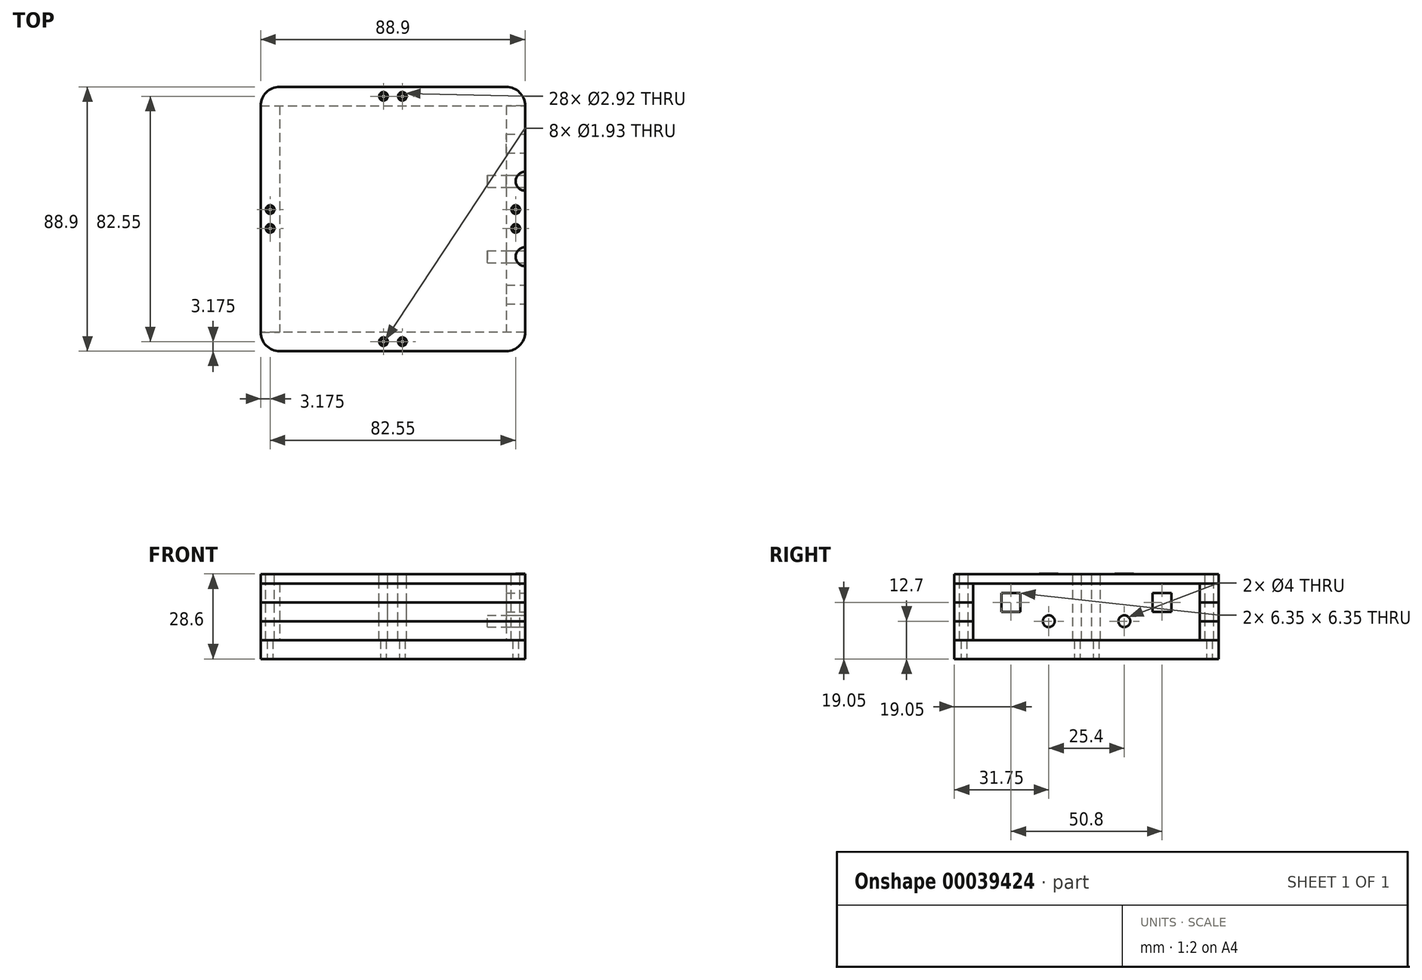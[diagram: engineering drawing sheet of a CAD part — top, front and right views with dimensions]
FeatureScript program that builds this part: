
annotation { "Feature Type Name" : "Feature", "Feature Type Description" : "" }
export const myFeature = defineFeature(function(context is Context, id is Id, definition is map)
    precondition{}
    {
        {
            var Q0;
            Q0=qCreatedBy(makeId("Top.planeOp"),FACE);
            var sketch = newSketch(context, id + "F0", { "sketchPlane" : qUnion([Q0])});
            skLineSegment(sketch, "E0.rect.bottom", {"start": v(38.1, 44.45) * mm, "end": v(-38.1, 44.45) * mm});
            skLineSegment(sketch, "E0.rect.top", {"start": v(38.1, -44.45) * mm, "end": v(-38.1, -44.45) * mm});
            skLineSegment(sketch, "E0.rect.left", {"start": v(44.45, 38.1) * mm, "end": v(44.45, -38.1) * mm});
            skLineSegment(sketch, "E0.rect.right", {"start": v(-44.45, 38.1) * mm, "end": v(-44.45, -38.1) * mm});
            skPoint(sketch, "E0.rect.middle", {"position": v(0, 0) * mm});
            skPoint(sketch, "E1.visualSharp", {"position": v(-44.45, 44.45) * mm});
            skArc(sketch, "E1.filletArc", {"start": v(-38.1, 44.45) * mm, "mid": v(-42.6, 42.6) * mm, "end": v(-44.45, 38.1) * mm});
            skPoint(sketch, "E2.visualSharp", {"position": v(44.45, 44.45) * mm});
            skArc(sketch, "E2.filletArc", {"start": v(44.45, 38.1) * mm, "mid": v(42.6, 42.6) * mm, "end": v(38.1, 44.45) * mm});
            skPoint(sketch, "E3.visualSharp", {"position": v(44.45, -44.45) * mm});
            skArc(sketch, "E3.filletArc", {"start": v(38.1, -44.45) * mm, "mid": v(42.6, -42.6) * mm, "end": v(44.45, -38.1) * mm});
            skPoint(sketch, "E4.visualSharp", {"position": v(-44.45, -44.45) * mm});
            skArc(sketch, "E4.filletArc", {"start": v(-44.45, -38.1) * mm, "mid": v(-42.6, -42.6) * mm, "end": v(-38.1, -44.45) * mm});
            skSolve(sketch);
        }
        {
            var Q0;
            Q0 = qSketchRegion(id + "F0", true);
            extrude(context, id + "F1", {"entities" : qUnion([Q0]), "depth" : 6.35 * mm});
        }
        {
            var Q0;
            Q0=makeQuery(id+"F1.opExtrude","CAP_FACE",FACE,{"disambiguationData":[OSD([sQuery(id+"F0.wireOp",EDGE,"E0.rect.bottom"),sQuery(id+"F0.wireOp",EDGE,"E0.rect.top"),sQuery(id+"F0.wireOp",EDGE,"E0.rect.left"),sQuery(id+"F0.wireOp",EDGE,"E0.rect.right"),sQuery(id+"F0.wireOp",EDGE,"E1.filletArc"),sQuery(id+"F0.wireOp",EDGE,"E2.filletArc"),sQuery(id+"F0.wireOp",EDGE,"E3.filletArc"),sQuery(id+"F0.wireOp",EDGE,"E4.filletArc")])],"isStart":false});
            var sketch = newSketch(context, id + "F2", { "sketchPlane" : qUnion([Q0])});
            skLineSegment(sketch, "E5.bottom", {"start": v(-44.45, 38.1) * mm, "end": v(-38.1, 38.1) * mm});
            skLineSegment(sketch, "E5.top", {"start": v(-44.45, -38.1) * mm, "end": v(-38.1, -38.1) * mm});
            skLineSegment(sketch, "E5.left", {"start": v(-44.45, 38.1) * mm, "end": v(-44.45, -38.1) * mm});
            skLineSegment(sketch, "E5.right", {"start": v(-38.1, 38.1) * mm, "end": v(-38.1, -38.1) * mm});
            skLineSegment(sketch, "E6.bottom", {"start": v(44.45, 38.1) * mm, "end": v(38.1, 38.1) * mm});
            skLineSegment(sketch, "E6.top", {"start": v(44.45, -38.1) * mm, "end": v(38.1, -38.1) * mm});
            skLineSegment(sketch, "E6.left", {"start": v(44.45, 38.1) * mm, "end": v(44.45, -38.1) * mm});
            skLineSegment(sketch, "E6.right", {"start": v(38.1, 38.1) * mm, "end": v(38.1, -38.1) * mm});
            skSolve(sketch);
        }
        {
            var Q0;
            Q0 = qSketchRegion(id + "F2", true);
            extrude(context, id + "F3", {"entities" : qUnion([Q0]), "depth" : 19.05 * mm});
        }
        {
            var Q0;
            Q0=makeQuery(id+"F1.opExtrude","CAP_FACE",FACE,{"disambiguationData":[OSD([sQuery(id+"F0.wireOp",EDGE,"E0.rect.bottom"),sQuery(id+"F0.wireOp",EDGE,"E0.rect.top"),sQuery(id+"F0.wireOp",EDGE,"E0.rect.left"),sQuery(id+"F0.wireOp",EDGE,"E0.rect.right"),sQuery(id+"F0.wireOp",EDGE,"E1.filletArc"),sQuery(id+"F0.wireOp",EDGE,"E2.filletArc"),sQuery(id+"F0.wireOp",EDGE,"E3.filletArc"),sQuery(id+"F0.wireOp",EDGE,"E4.filletArc")])],"isStart":false});
            var sketch = newSketch(context, id + "F4", { "sketchPlane" : qUnion([Q0])});
            skArc(sketch, "E7.0", {"start": v(-38.1, 44.45) * mm, "mid": v(-42.6, 42.6) * mm, "end": v(-44.45, 38.1) * mm});
            skLineSegment(sketch, "E8.0", {"start": v(38.1, 44.45) * mm, "end": v(-38.1, 44.45) * mm});
            skArc(sketch, "E9.0", {"start": v(44.45, 38.1) * mm, "mid": v(42.6, 42.6) * mm, "end": v(38.1, 44.45) * mm});
            skLineSegment(sketch, "E10", {"start": v(-38.1, 38.1) * mm, "end": v(38.1, 38.1) * mm});
            skLineSegment(sketch, "E11.0", {"start": v(-44.45, -38.1) * mm, "end": v(-38.1, -38.1) * mm});
            skArc(sketch, "E12.0", {"start": v(-44.45, -38.1) * mm, "mid": v(-42.6, -42.6) * mm, "end": v(-38.1, -44.45) * mm});
            skLineSegment(sketch, "E13.0", {"start": v(38.1, -44.45) * mm, "end": v(-38.1, -44.45) * mm});
            skArc(sketch, "E14.0", {"start": v(38.1, -44.45) * mm, "mid": v(42.6, -42.6) * mm, "end": v(44.45, -38.1) * mm});
            skLineSegment(sketch, "E15", {"start": v(-38.1, -38.1) * mm, "end": v(38.1, -38.1) * mm});
            skLineSegment(sketch, "E16", {"start": v(38.1, -38.1) * mm, "end": v(44.45, -38.1) * mm});
            skLineSegment(sketch, "E17", {"start": v(-38.1, -38.1) * mm, "end": v(-44.45, -38.1) * mm});
            skLineSegment(sketch, "E18", {"start": v(-44.45, 38.1) * mm, "end": v(-38.1, 38.1) * mm});
            skLineSegment(sketch, "E19", {"start": v(38.1, 38.1) * mm, "end": v(44.45, 38.1) * mm});
            skSolve(sketch);
        }
        {
            var Q0;
            Q0 = qSketchRegion(id + "F4", true);
            extrude(context, id + "F5", {"entities" : qUnion([Q0]), "depth" : 12.7 * mm});
        }
        {
            var Q0;
            Q0=makeQuery(id+"F5.opExtrude","CAP_FACE",FACE,{"disambiguationData":[OSD([sQuery(id+"F4.wireOp",EDGE,"E7.0"),sQuery(id+"F4.wireOp",EDGE,"E8.0"),sQuery(id+"F4.wireOp",EDGE,"E9.0"),sQuery(id+"F4.wireOp",EDGE,"E10"),sQuery(id+"F4.wireOp",EDGE,"E18"),sQuery(id+"F4.wireOp",EDGE,"E19")])],"isStart":false});
            var sketch = newSketch(context, id + "F6", { "sketchPlane" : qUnion([Q0])});
            skLineSegment(sketch, "E20.0.0", {"start": v(-44.45, 38.1) * mm, "end": v(44.45, 38.1) * mm});
            skArc(sketch, "E20.0.1", {"start": v(44.45, 38.1) * mm, "mid": v(42.6, 42.6) * mm, "end": v(38.1, 44.45) * mm});
            skLineSegment(sketch, "E20.0.2", {"start": v(38.1, 44.45) * mm, "end": v(-38.1, 44.45) * mm});
            skArc(sketch, "E20.0.3", {"start": v(-38.1, 44.45) * mm, "mid": v(-42.6, 42.6) * mm, "end": v(-44.45, 38.1) * mm});
            skLineSegment(sketch, "E21.0.0", {"start": v(44.45, -38.1) * mm, "end": v(-44.45, -38.1) * mm});
            skArc(sketch, "E21.0.1", {"start": v(-44.45, -38.1) * mm, "mid": v(-42.6, -42.6) * mm, "end": v(-38.1, -44.45) * mm});
            skLineSegment(sketch, "E21.0.2", {"start": v(-38.1, -44.45) * mm, "end": v(38.1, -44.45) * mm});
            skArc(sketch, "E21.0.3", {"start": v(38.1, -44.45) * mm, "mid": v(42.6, -42.6) * mm, "end": v(44.45, -38.1) * mm});
            skSolve(sketch);
        }
        {
            var Q0;
            Q0 = qSketchRegion(id + "F6", true);
            extrude(context, id + "F7", {"entities" : qUnion([Q0]), "depth" : 6.35 * mm});
        }
        {
            var Q0;
            Q0=makeQuery(id+"F3.opExtrude","CAP_FACE",FACE,{"disambiguationData":[OSD([sQuery(id+"F2.wireOp",EDGE,"E5.bottom"),sQuery(id+"F2.wireOp",EDGE,"E5.top"),sQuery(id+"F2.wireOp",EDGE,"E5.left"),sQuery(id+"F2.wireOp",EDGE,"E5.right")])],"isStart":false});
            var sketch = newSketch(context, id + "F8", { "sketchPlane" : qUnion([Q0])});
            skArc(sketch, "E22.0.0", {"start": v(44.45, 38.1) * mm, "mid": v(42.6, 42.6) * mm, "end": v(38.1, 44.45) * mm});
            skLineSegment(sketch, "E22.0.1", {"start": v(38.1, 44.45) * mm, "end": v(-38.1, 44.45) * mm});
            skArc(sketch, "E22.0.2", {"start": v(-38.1, 44.45) * mm, "mid": v(-42.6, 42.6) * mm, "end": v(-44.45, 38.1) * mm});
            skLineSegment(sketch, "E22.0.3", {"start": v(-44.45, 38.1) * mm, "end": v(-44.45, -38.1) * mm});
            skArc(sketch, "E22.0.4", {"start": v(-44.45, -38.1) * mm, "mid": v(-42.6, -42.6) * mm, "end": v(-38.1, -44.45) * mm});
            skLineSegment(sketch, "E22.0.5", {"start": v(-38.1, -44.45) * mm, "end": v(38.1, -44.45) * mm});
            skArc(sketch, "E22.0.6", {"start": v(38.1, -44.45) * mm, "mid": v(42.6, -42.6) * mm, "end": v(44.45, -38.1) * mm});
            skLineSegment(sketch, "E22.0.7", {"start": v(44.45, -38.1) * mm, "end": v(44.45, 38.1) * mm});
            skSolve(sketch);
        }
        {
            var Q0;
            Q0 = qSketchRegion(id + "F8", true);
            extrude(context, id + "F9", {"entities" : qUnion([Q0]), "depth" : 3.17 * mm});
        }
        {
            var Q0;
            Q0=makeQuery(id+"F3.opExtrude","SWEPT_FACE",FACE,{"disambiguationData":[OSD([sQuery(id+"F2.wireOp",EDGE,"E6.left")])]});
            var sketch = newSketch(context, id + "F10", { "sketchPlane" : qUnion([Q0])});
            skLineSegment(sketch, "E23.rect.bottom", {"start": v(22.22, 22.23) * mm, "end": v(28.57, 22.23) * mm});
            skLineSegment(sketch, "E23.rect.top", {"start": v(22.22, 15.88) * mm, "end": v(28.57, 15.88) * mm});
            skLineSegment(sketch, "E23.rect.left", {"start": v(22.22, 22.23) * mm, "end": v(22.22, 15.88) * mm});
            skLineSegment(sketch, "E23.rect.right", {"start": v(28.57, 22.23) * mm, "end": v(28.57, 15.88) * mm});
            skPoint(sketch, "E23.rect.middle", {"position": v(25.4, 19.05) * mm});
            skLineSegment(sketch, "E24.rect.bottom", {"start": v(-22.22, 15.88) * mm, "end": v(-28.57, 15.88) * mm});
            skLineSegment(sketch, "E24.rect.top", {"start": v(-22.22, 22.23) * mm, "end": v(-28.57, 22.23) * mm});
            skLineSegment(sketch, "E24.rect.left", {"start": v(-22.22, 15.88) * mm, "end": v(-22.22, 22.23) * mm});
            skLineSegment(sketch, "E24.rect.right", {"start": v(-28.57, 15.88) * mm, "end": v(-28.57, 22.23) * mm});
            skPoint(sketch, "E24.rect.middle", {"position": v(-25.4, 19.05) * mm});
            skCircle(sketch, "E25", {"center": v(-12.7, 12.7) * mm, "radius": 2 * mm});
            skCircle(sketch, "E26", {"center": v(12.7, 12.7) * mm, "radius": 2 * mm});
            skLineSegment(sketch, "E27", {"start": v(0, 25.4) * mm, "end": v(0, 6.35) * mm});
            skSolve(sketch);
        }
        {
            var Q0;
            Q0 = qSketchRegion(id + "F10", true);
            extrude(context, id + "F11", {"entities" : qUnion([Q0]), "operationType" : NewBodyOperationType.REMOVE, "oppositeDirection" : true, "depth" : 25.4 * mm});
        }
        {
            var Q0;
            Q0=makeQuery(id+"F9.opExtrude","CAP_FACE",FACE,{"disambiguationData":[OSD([sQuery(id+"F8.wireOp",EDGE,"E22.0.0"),sQuery(id+"F8.wireOp",EDGE,"E22.0.1"),sQuery(id+"F8.wireOp",EDGE,"E22.0.2"),sQuery(id+"F8.wireOp",EDGE,"E22.0.3"),sQuery(id+"F8.wireOp",EDGE,"E22.0.4"),sQuery(id+"F8.wireOp",EDGE,"E22.0.5"),sQuery(id+"F8.wireOp",EDGE,"E22.0.6"),sQuery(id+"F8.wireOp",EDGE,"E22.0.7")])],"isStart":false});
            var sketch = newSketch(context, id + "F12", { "sketchPlane" : qUnion([Q0])});
            skCircle(sketch, "E28", {"center": v(-41.28, 3.17) * mm, "radius": 1.46 * mm});
            skCircle(sketch, "E29", {"center": v(-41.28, -3.18) * mm, "radius": 1.46 * mm});
            skLineSegment(sketch, "E30", {"start": v(-44.45, 0) * mm, "end": v(44.45, 0) * mm});
            skLineSegment(sketch, "E31", {"start": v(0, 44.45) * mm, "end": v(0, -44.45) * mm});
            skCircle(sketch, "E32", {"center": v(-3.18, 41.27) * mm, "radius": 1.46 * mm});
            skCircle(sketch, "E33", {"center": v(3.17, 41.27) * mm, "radius": 1.46 * mm});
            skCircle(sketch, "E34", {"center": v(-3.18, -41.28) * mm, "radius": 1.46 * mm});
            skCircle(sketch, "E35", {"center": v(3.18, -41.28) * mm, "radius": 1.46 * mm});
            skCircle(sketch, "E36", {"center": v(41.28, 3.18) * mm, "radius": 1.46 * mm});
            skCircle(sketch, "E37", {"center": v(41.28, -3.17) * mm, "radius": 1.46 * mm});
            skSolve(sketch);
        }
        {
            var Q0;
            Q0 = qSketchRegion(id + "F12", true);
            extrude(context, id + "F13", {"entities" : qUnion([Q0]), "operationType" : NewBodyOperationType.REMOVE, "oppositeDirection" : true, "depth" : 22.22 * mm});
        }
        {
            var Q0;
            Q0=makeQuery(id+"F1.opExtrude","CAP_FACE",FACE,{"disambiguationData":[OSD([sQuery(id+"F0.wireOp",EDGE,"E0.rect.bottom"),sQuery(id+"F0.wireOp",EDGE,"E0.rect.top"),sQuery(id+"F0.wireOp",EDGE,"E0.rect.left"),sQuery(id+"F0.wireOp",EDGE,"E0.rect.right"),sQuery(id+"F0.wireOp",EDGE,"E1.filletArc"),sQuery(id+"F0.wireOp",EDGE,"E2.filletArc"),sQuery(id+"F0.wireOp",EDGE,"E3.filletArc"),sQuery(id+"F0.wireOp",EDGE,"E4.filletArc")])],"isStart":true});
            var sketch = newSketch(context, id + "F14", { "sketchPlane" : qUnion([Q0])});
            skCircle(sketch, "E38.0", {"center": v(-3.18, 41.28) * mm, "radius": 1.46 * mm});
            skCircle(sketch, "E39.0", {"center": v(3.18, 41.28) * mm, "radius": 1.46 * mm});
            skCircle(sketch, "E40.0", {"center": v(41.28, 3.17) * mm, "radius": 1.46 * mm});
            skCircle(sketch, "E41.0", {"center": v(41.28, -3.18) * mm, "radius": 1.46 * mm});
            skCircle(sketch, "E42.0", {"center": v(-41.28, 3.18) * mm, "radius": 1.46 * mm});
            skCircle(sketch, "E43.0", {"center": v(-41.28, -3.17) * mm, "radius": 1.46 * mm});
            skCircle(sketch, "E44.0", {"center": v(-3.18, -41.27) * mm, "radius": 1.46 * mm});
            skCircle(sketch, "E45.0", {"center": v(3.17, -41.27) * mm, "radius": 1.46 * mm});
            skCircle(sketch, "E46", {"center": v(-41.28, 3.18) * mm, "radius": 0.97 * mm});
            skCircle(sketch, "E47", {"center": v(-41.28, -3.17) * mm, "radius": 0.97 * mm});
            skCircle(sketch, "E48", {"center": v(-3.18, 41.28) * mm, "radius": 0.97 * mm});
            skCircle(sketch, "E49", {"center": v(3.18, 41.28) * mm, "radius": 0.97 * mm});
            skCircle(sketch, "E50", {"center": v(41.28, 3.17) * mm, "radius": 0.97 * mm});
            skCircle(sketch, "E51", {"center": v(41.28, -3.18) * mm, "radius": 0.97 * mm});
            skCircle(sketch, "E52", {"center": v(-3.18, -41.27) * mm, "radius": 0.97 * mm});
            skCircle(sketch, "E53", {"center": v(3.17, -41.27) * mm, "radius": 0.97 * mm});
            skSolve(sketch);
        }
        {
            var Q0;
            Q0=makeQuery(id+"F14.imprint","IMPRINT",FACE,{"disambiguationData":[TD([[makeQuery(id+"F14.imprint","IMPRINT",EDGE,{"derivedFrom":sQuery(id+"F14.wireOp",EDGE,"E52")}),1.0]])]});
            var Q1;
            Q1=makeQuery(id+"F14.imprint","IMPRINT",FACE,{"disambiguationData":[TD([[makeQuery(id+"F14.imprint","IMPRINT",EDGE,{"derivedFrom":sQuery(id+"F14.wireOp",EDGE,"E53")}),1.0]])]});
            var Q2;
            Q2=makeQuery(id+"F14.imprint","IMPRINT",FACE,{"disambiguationData":[TD([[makeQuery(id+"F14.imprint","IMPRINT",EDGE,{"derivedFrom":sQuery(id+"F14.wireOp",EDGE,"E46")}),1.0]])]});
            var Q3;
            Q3=makeQuery(id+"F14.imprint","IMPRINT",FACE,{"disambiguationData":[TD([[makeQuery(id+"F14.imprint","IMPRINT",EDGE,{"derivedFrom":sQuery(id+"F14.wireOp",EDGE,"E47")}),1.0]])]});
            var Q4;
            Q4=makeQuery(id+"F14.imprint","IMPRINT",FACE,{"disambiguationData":[TD([[makeQuery(id+"F14.imprint","IMPRINT",EDGE,{"derivedFrom":sQuery(id+"F14.wireOp",EDGE,"E51")}),1.0]])]});
            var Q5;
            Q5=makeQuery(id+"F14.imprint","IMPRINT",FACE,{"disambiguationData":[TD([[makeQuery(id+"F14.imprint","IMPRINT",EDGE,{"derivedFrom":sQuery(id+"F14.wireOp",EDGE,"E50")}),1.0]])]});
            var Q6;
            Q6=makeQuery(id+"F14.imprint","IMPRINT",FACE,{"disambiguationData":[TD([[makeQuery(id+"F14.imprint","IMPRINT",EDGE,{"derivedFrom":sQuery(id+"F14.wireOp",EDGE,"E49")}),1.0]])]});
            var Q7;
            Q7=makeQuery(id+"F14.imprint","IMPRINT",FACE,{"disambiguationData":[TD([[makeQuery(id+"F14.imprint","IMPRINT",EDGE,{"derivedFrom":sQuery(id+"F14.wireOp",EDGE,"E48")}),1.0]])]});
            extrude(context, id + "F15", {"entities" : qUnion([Q0, Q1, Q2, Q3, Q4, Q5, Q6, Q7]), "operationType" : NewBodyOperationType.REMOVE, "oppositeDirection" : true, "depth" : 6.35 * mm});
        }
        {
            var Q0;
            Q0=makeQuery(id+"F9.opExtrude","CAP_FACE",FACE,{"disambiguationData":[OSD([sQuery(id+"F8.wireOp",EDGE,"E22.0.0"),sQuery(id+"F8.wireOp",EDGE,"E22.0.1"),sQuery(id+"F8.wireOp",EDGE,"E22.0.2"),sQuery(id+"F8.wireOp",EDGE,"E22.0.3"),sQuery(id+"F8.wireOp",EDGE,"E22.0.4"),sQuery(id+"F8.wireOp",EDGE,"E22.0.5"),sQuery(id+"F8.wireOp",EDGE,"E22.0.6"),sQuery(id+"F8.wireOp",EDGE,"E22.0.7")])],"isStart":false});
            var sketch = newSketch(context, id + "F16", { "sketchPlane" : qUnion([Q0])});
            skLineSegment(sketch, "E54", {"start": v(44.45, 0) * mm, "end": v(15.45, 0) * mm});
            skArc(sketch, "E55", {"start": v(44.45, 15.88) * mm, "mid": v(41.28, 12.7) * mm, "end": v(44.45, 9.53) * mm});
            skArc(sketch, "E56", {"start": v(44.45, -9.52) * mm, "mid": v(41.28, -12.7) * mm, "end": v(44.45, -15.88) * mm});
            skLineSegment(sketch, "E57", {"start": v(44.45, 15.88) * mm, "end": v(44.45, -15.88) * mm});
            skSolve(sketch);
        }
        {
            var Q0;
            Q0 = qSketchRegion(id + "F16", true);
            extrude(context, id + "F17", {"entities" : qUnion([Q0]), "depth" : 0.03 * mm});
        }
        {
            var Q0;
            Q0=makeQuery(id+"F3.opExtrude","SWEPT_FACE",FACE,{"disambiguationData":[OSD([sQuery(id+"F2.wireOp",EDGE,"E6.left")])]});
            var sketch = newSketch(context, id + "F18", { "sketchPlane" : qUnion([Q0])});
            skLineSegment(sketch, "E58.0", {"start": v(22.22, 15.88) * mm, "end": v(28.57, 15.88) * mm});
            skLineSegment(sketch, "E59.0", {"start": v(28.57, 22.23) * mm, "end": v(28.57, 15.88) * mm});
            skLineSegment(sketch, "E60.0", {"start": v(22.22, 22.23) * mm, "end": v(28.57, 22.23) * mm});
            skLineSegment(sketch, "E61.0", {"start": v(22.22, 22.23) * mm, "end": v(22.22, 15.88) * mm});
            skLineSegment(sketch, "E62.0", {"start": v(-22.22, 15.88) * mm, "end": v(-22.22, 22.23) * mm});
            skLineSegment(sketch, "E63.0", {"start": v(-22.22, 15.88) * mm, "end": v(-28.57, 15.88) * mm});
            skLineSegment(sketch, "E64.0", {"start": v(-28.57, 15.88) * mm, "end": v(-28.57, 22.23) * mm});
            skLineSegment(sketch, "E65.0", {"start": v(-22.22, 22.23) * mm, "end": v(-28.57, 22.23) * mm});
            skSolve(sketch);
        }
        {
            var Q0;
            Q0 = qSketchRegion(id + "F18", true);
            extrude(context, id + "F19", {"entities" : qUnion([Q0]), "oppositeDirection" : true, "depth" : 6.35 * mm});
        }
        {
            var Q0;
            Q0=makeQuery(id+"F3.opExtrude","SWEPT_FACE",FACE,{"disambiguationData":[OSD([sQuery(id+"F2.wireOp",EDGE,"E6.left")])]});
            var sketch = newSketch(context, id + "F20", { "sketchPlane" : qUnion([Q0])});
            skCircle(sketch, "E66.0", {"center": v(12.7, 12.7) * mm, "radius": 2 * mm});
            skCircle(sketch, "E67.0", {"center": v(-12.7, 12.7) * mm, "radius": 2 * mm});
            skSolve(sketch);
        }
        {
            var Q0;
            Q0 = qSketchRegion(id + "F20", true);
            extrude(context, id + "F21", {"entities" : qUnion([Q0]), "oppositeDirection" : true, "depth" : 12.7 * mm});
        }
        {
            var Q0;
            Q0=makeQuery(id+"F7.opExtrude","SWEPT_BODY",BODY,{"disambiguationData":[OSD([sQuery(id+"F6.wireOp",EDGE,"E20.0.0"),sQuery(id+"F6.wireOp",EDGE,"E20.0.1"),sQuery(id+"F6.wireOp",EDGE,"E20.0.2"),sQuery(id+"F6.wireOp",EDGE,"E20.0.3")])]});
            transform(context, id + "F22", {"entities" : qUnion([Q0]), "transformType" : TransformType.TRANSLATION_3D, "dx" : 0 * mm, "dy" : 0 * mm, "dz" : -6.35 * mm, "makeCopy" : true});
        }
        {
            var Q0;
            Q0=makeQuery(id+"F22.opPattern","COPY",BODY,{"derivedFrom":makeQuery(id+"F7.opExtrude","SWEPT_BODY",BODY,{"disambiguationData":[OSD([sQuery(id+"F6.wireOp",EDGE,"E20.0.0"),sQuery(id+"F6.wireOp",EDGE,"E20.0.1"),sQuery(id+"F6.wireOp",EDGE,"E20.0.2"),sQuery(id+"F6.wireOp",EDGE,"E20.0.3")])]}),"instanceName":"1"});
            transform(context, id + "F23", {"entities" : qUnion([Q0]), "transformType" : TransformType.TRANSLATION_3D, "dx" : 0 * mm, "dy" : 0 * mm, "dz" : -6.35 * mm, "makeCopy" : true});
        }
        {
            var Q0;
            Q0=makeQuery(id+"F7.opExtrude","SWEPT_BODY",BODY,{"disambiguationData":[OSD([sQuery(id+"F6.wireOp",EDGE,"E21.0.0"),sQuery(id+"F6.wireOp",EDGE,"E21.0.1"),sQuery(id+"F6.wireOp",EDGE,"E21.0.2"),sQuery(id+"F6.wireOp",EDGE,"E21.0.3")])]});
            transform(context, id + "F24", {"entities" : qUnion([Q0]), "transformType" : TransformType.TRANSLATION_3D, "dx" : 0 * mm, "dy" : 0 * mm, "dz" : -12.7 * mm, "makeCopy" : true});
        }
        {
            var Q0;
            Q0=makeQuery(id+"F24.opPattern","COPY",BODY,{"derivedFrom":makeQuery(id+"F7.opExtrude","SWEPT_BODY",BODY,{"disambiguationData":[OSD([sQuery(id+"F6.wireOp",EDGE,"E21.0.0"),sQuery(id+"F6.wireOp",EDGE,"E21.0.1"),sQuery(id+"F6.wireOp",EDGE,"E21.0.2"),sQuery(id+"F6.wireOp",EDGE,"E21.0.3")])]}),"instanceName":"1"});
            transform(context, id + "F25", {"entities" : qUnion([Q0]), "transformType" : TransformType.TRANSLATION_3D, "dx" : 0 * mm, "dy" : 0 * mm, "dz" : 6.35 * mm, "makeCopy" : true});
        }
    });
